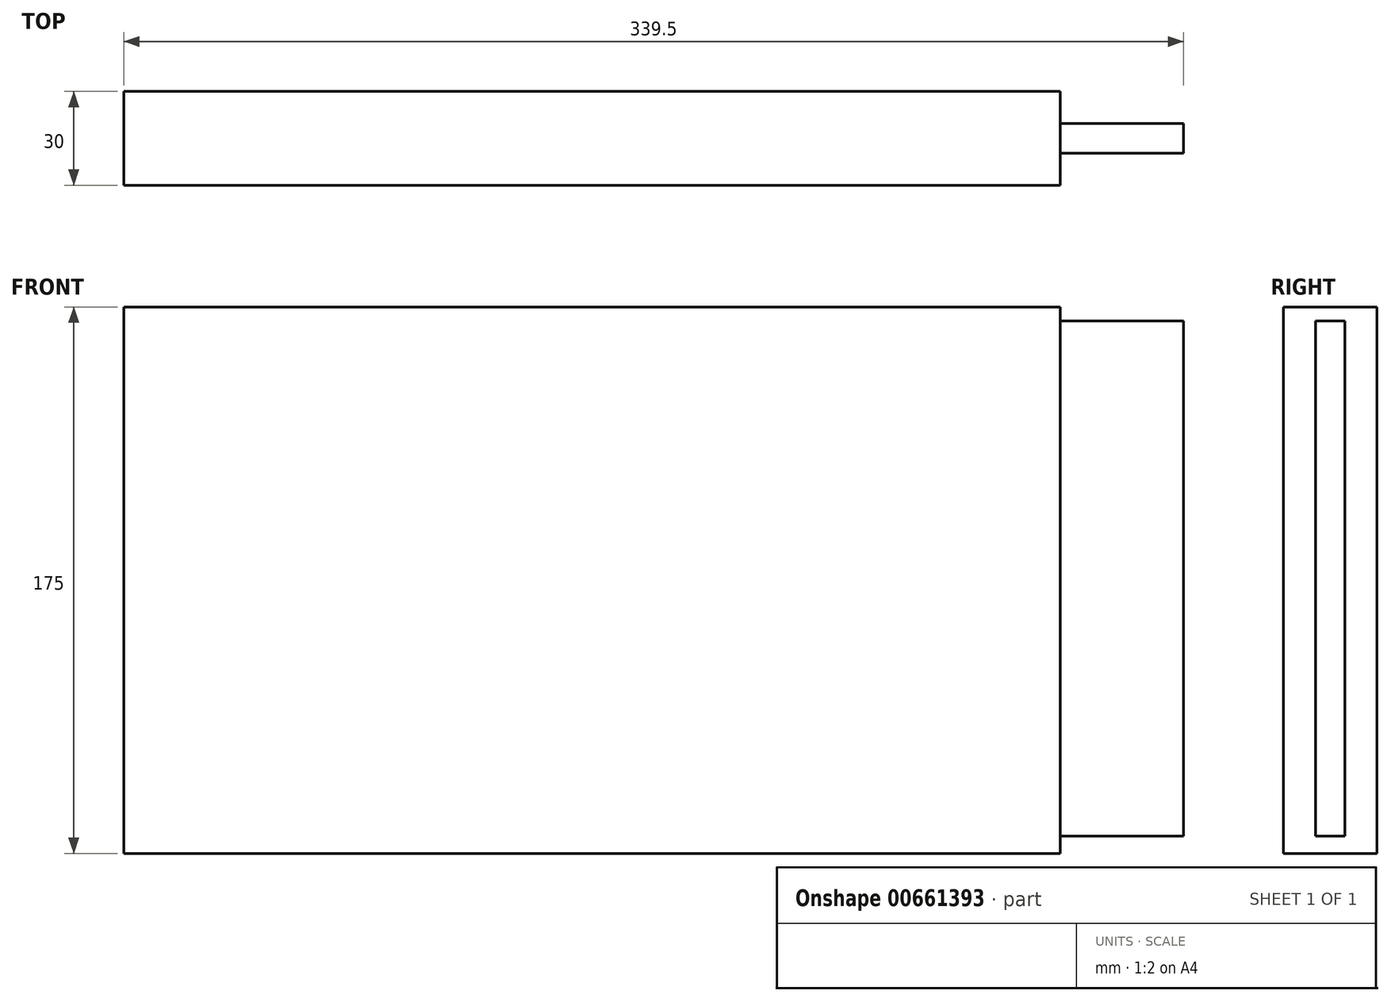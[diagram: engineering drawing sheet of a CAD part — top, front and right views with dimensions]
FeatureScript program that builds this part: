
annotation { "Feature Type Name" : "Feature", "Feature Type Description" : "" }
export const myFeature = defineFeature(function(context is Context, id is Id, definition is map)
    precondition{}
    {
        {
            var Q0;
            Q0=qCreatedBy(makeId("Front.planeOp"),FACE);
            var sketch = newSketch(context, id + "F0", { "sketchPlane" : qUnion([Q0])});
            skLineSegment(sketch, "E0.bottom", {"start": v(150, -87.5) * mm, "end": v(-150, -87.5) * mm});
            skLineSegment(sketch, "E0.top", {"start": v(150, 87.5) * mm, "end": v(-150, 87.5) * mm});
            skLineSegment(sketch, "E0.left", {"start": v(150, -87.5) * mm, "end": v(150, 87.5) * mm});
            skLineSegment(sketch, "E0.right", {"start": v(-150, -87.5) * mm, "end": v(-150, 87.5) * mm});
            skPoint(sketch, "E0.middle", {"position": v(0, 0) * mm});
            skSolve(sketch);
        }
        {
            var Q0;
            Q0=makeQuery(id+"F0.imprint","IMPRINT",FACE,{"disambiguationData":[TD([[makeQuery(id+"F0.imprint","IMPRINT",EDGE,{"derivedFrom":sQuery(id+"F0.wireOp",EDGE,"E0.bottom")}),-1.0]])]});
            extrude(context, id + "F1", {"entities" : qUnion([Q0]), "depth" : 30 * mm, "offsetDistance" : 25 * mm});
        }
        {
            var Q0;
            Q0=makeQuery(id+"F1.opExtrude","SWEPT_FACE",FACE,{"disambiguationData":[OSD([sQuery(id+"F0.wireOp",EDGE,"E0.left")])]});
            var sketch = newSketch(context, id + "F2", { "sketchPlane" : qUnion([Q0])});
            skLineSegment(sketch, "E1.bottom", {"start": v(-19.75, -82) * mm, "end": v(-10.25, -82) * mm});
            skLineSegment(sketch, "E1.top", {"start": v(-19.75, 83) * mm, "end": v(-10.25, 83) * mm});
            skLineSegment(sketch, "E1.left", {"start": v(-19.75, -82) * mm, "end": v(-19.75, 83) * mm});
            skLineSegment(sketch, "E1.right", {"start": v(-10.25, -82) * mm, "end": v(-10.25, 83) * mm});
            skLineSegment(sketch, "E2", {"start": v(-30, -82) * mm, "end": v(-19.75, -82) * mm});
            skLineSegment(sketch, "E3", {"start": v(-30, -87.5) * mm, "end": v(-30, -82) * mm});
            skLineSegment(sketch, "E4", {"start": v(-19.75, 83) * mm, "end": v(-30, 83) * mm});
            skLineSegment(sketch, "E5", {"start": v(-30, 83) * mm, "end": v(-19.75, 83) * mm});
            skLineSegment(sketch, "E6", {"start": v(-30, 83) * mm, "end": v(-30, 87.5) * mm});
            skLineSegment(sketch, "E7", {"start": v(-10.25, 83) * mm, "end": v(0, 83) * mm});
            skSolve(sketch);
        }
        {
            var Q0;
            Q0=makeQuery(id+"F2.imprint","IMPRINT",FACE,{"disambiguationData":[TD([[makeQuery(id+"F2.imprint","IMPRINT",EDGE,{"derivedFrom":sQuery(id+"F2.wireOp",EDGE,"E1.bottom")}),1.0]])]});
            extrude(context, id + "F3", {"entities" : qUnion([Q0]), "operationType" : NewBodyOperationType.ADD, "depth" : 39.5 * mm, "offsetDistance" : 25 * mm});
        }
    });
